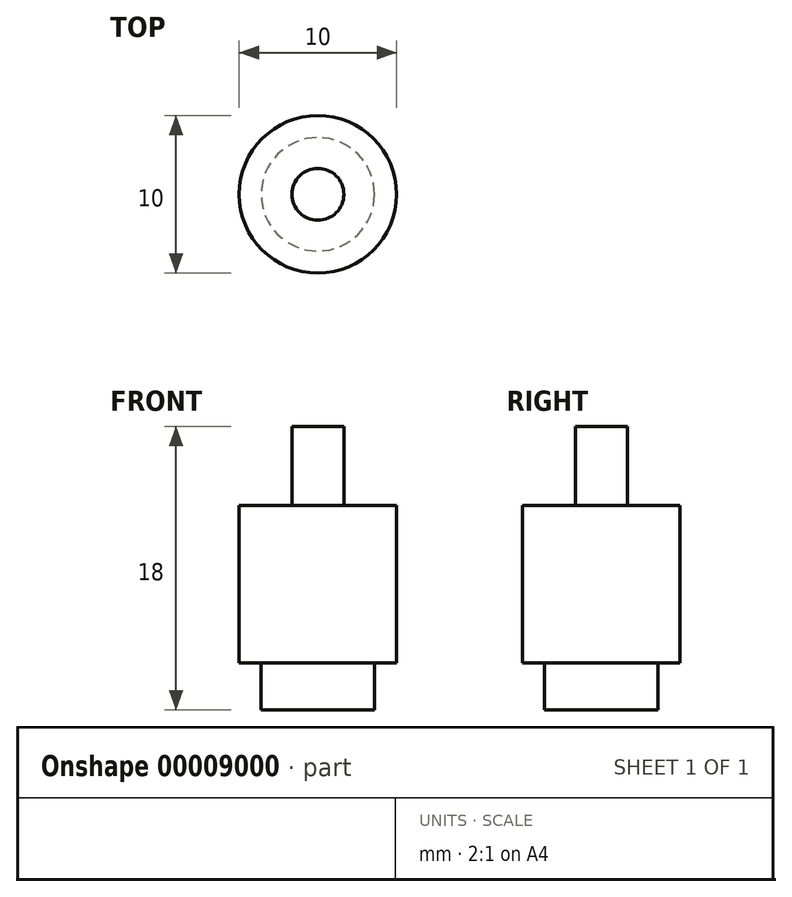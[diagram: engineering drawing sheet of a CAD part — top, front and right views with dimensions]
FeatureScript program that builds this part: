
annotation { "Feature Type Name" : "Feature", "Feature Type Description" : "" }
export const myFeature = defineFeature(function(context is Context, id is Id, definition is map)
    precondition{}
    {
        {
            var Q0;
            Q0=qCreatedBy(makeId("Top.planeOp"),FACE);
            var sketch = newSketch(context, id + "F0", { "sketchPlane" : qUnion([Q0])});
            skCircle(sketch, "E0", {"center": v(0, 0) * mm, "radius": 5 * mm});
            skSolve(sketch);
        }
        {
            var Q0;
            Q0 = qSketchRegion(id + "F0", true);
            extrude(context, id + "F1", {"entities" : qUnion([Q0]), "endBound" : BoundingType.SYMMETRIC, "depth" : 10 * mm});
        }
        {
            var Q0;
            Q0=makeQuery(id+"F1.opExtrude","CAP_FACE",FACE,{"disambiguationData":[OSD([sQuery(id+"F0.wireOp",EDGE,"E0")])],"isStart":true});
            var sketch = newSketch(context, id + "F2", { "sketchPlane" : qUnion([Q0])});
            skCircle(sketch, "E1", {"center": v(0, 0) * mm, "radius": 3.6 * mm});
            skSolve(sketch);
        }
        {
            var Q0;
            Q0 = qSketchRegion(id + "F2", true);
            extrude(context, id + "F3", {"entities" : qUnion([Q0]), "operationType" : NewBodyOperationType.ADD, "depth" : 3 * mm});
        }
        {
            var Q0;
            Q0=makeQuery(id+"F1.opExtrude","CAP_FACE",FACE,{"disambiguationData":[OSD([sQuery(id+"F0.wireOp",EDGE,"E0")])],"isStart":false});
            var sketch = newSketch(context, id + "F4", { "sketchPlane" : qUnion([Q0])});
            skCircle(sketch, "E2", {"center": v(0, 0) * mm, "radius": 1.65 * mm});
            skSolve(sketch);
        }
        {
            var Q0;
            Q0 = qSketchRegion(id + "F4", true);
            extrude(context, id + "F5", {"entities" : qUnion([Q0]), "operationType" : NewBodyOperationType.ADD, "depth" : 5 * mm});
        }
    });
